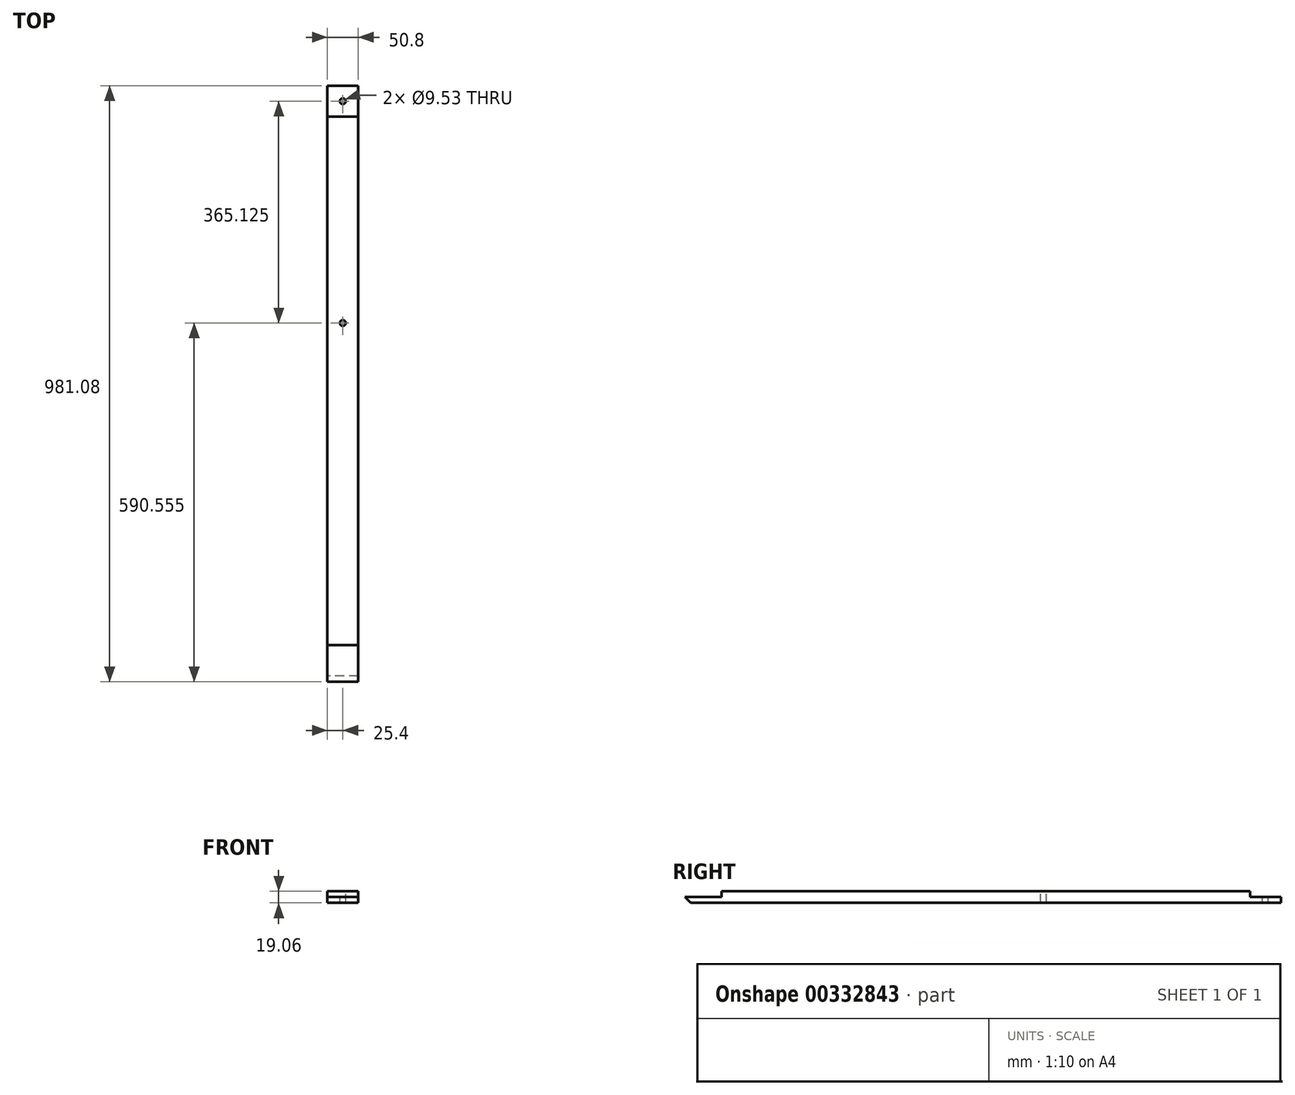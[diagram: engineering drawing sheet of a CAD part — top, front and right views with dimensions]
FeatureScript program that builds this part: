
annotation { "Feature Type Name" : "Feature", "Feature Type Description" : "" }
export const myFeature = defineFeature(function(context is Context, id is Id, definition is map)
    precondition{}
    {
        {
            var Q0;
            Q0=qCreatedBy(makeId("Right.planeOp"),FACE);
            var sketch = newSketch(context, id + "F0", { "sketchPlane" : qUnion([Q0])});
            skLineSegment(sketch, "E0.right", {"start": v(0, 9.53) * mm, "end": v(787.4, 9.53) * mm});
            skLineSegment(sketch, "E1", {"start": v(838.2, -9.52) * mm, "end": v(-33.3, -9.53) * mm});
            skLineSegment(sketch, "E2.bottom", {"start": v(838.2, 9.53) * mm, "end": v(838.2, 0) * mm});
            skLineSegment(sketch, "E2.top", {"start": v(787.4, 9.53) * mm, "end": v(787.4, 0) * mm});
            skLineSegment(sketch, "E2.right", {"start": v(838.2, 0) * mm, "end": v(787.4, 0) * mm});
            skPoint(sketch, "E2.left.start.orphan", {"position": v(838.2, 48.5) * mm});
            skPoint(sketch, "E3.orphan", {"position": v(787.4, 48.5) * mm});
            skLineSegment(sketch, "E4", {"start": v(0, 9.52) * mm, "end": v(-82.55, 9.52) * mm});
            skLineSegment(sketch, "E5", {"start": v(-142.88, 0) * mm, "end": v(-133.35, -9.53) * mm});
            skLineSegment(sketch, "E6", {"start": v(-33.3, -9.53) * mm, "end": v(-133.35, -9.53) * mm});
            skPoint(sketch, "E7.start.orphan", {"position": v(431.8, 9.53) * mm});
            skLineSegment(sketch, "E8", {"start": v(838.2, 0) * mm, "end": v(838.2, -9.52) * mm});
            skLineSegment(sketch, "E9.bottom", {"start": v(-142.88, 0) * mm, "end": v(-82.55, 0) * mm});
            skLineSegment(sketch, "E9.right", {"start": v(-82.55, 0) * mm, "end": v(-82.55, 9.52) * mm});
            skPoint(sketch, "E9.left.start.orphan", {"position": v(-211.72, 0) * mm});
            skPoint(sketch, "E10.orphan", {"position": v(-152.4, 9.52) * mm});
            skSolve(sketch);
        }
        {
            var Q0;
            Q0=qSketchRegion(id+"F0",true);
            extrude(context, id + "F1", {"entities" : qUnion([Q0]), "endBound" : BoundingType.SYMMETRIC, "depth" : 50.8 * mm});
        }
        {
            var Q0;
            Q0=qCreatedBy(makeId("Top.planeOp"),FACE);
            var sketch = newSketch(context, id + "F2", { "sketchPlane" : qUnion([Q0])});
            skCircle(sketch, "E11", {"center": v(0, 812.8) * mm, "radius": 4.76 * mm});
            skCircle(sketch, "E12", {"center": v(0, 447.67) * mm, "radius": 4.76 * mm});
            skSolve(sketch);
        }
        {
            var Q0;
            Q0 = qSketchRegion(id + "F2", true);
            extrude(context, id + "F3", {"entities" : qUnion([Q0]), "operationType" : NewBodyOperationType.REMOVE, "endBound" : BoundingType.SYMMETRIC, "oppositeDirection" : true, "depth" : 25.4 * mm});
        }
    });
